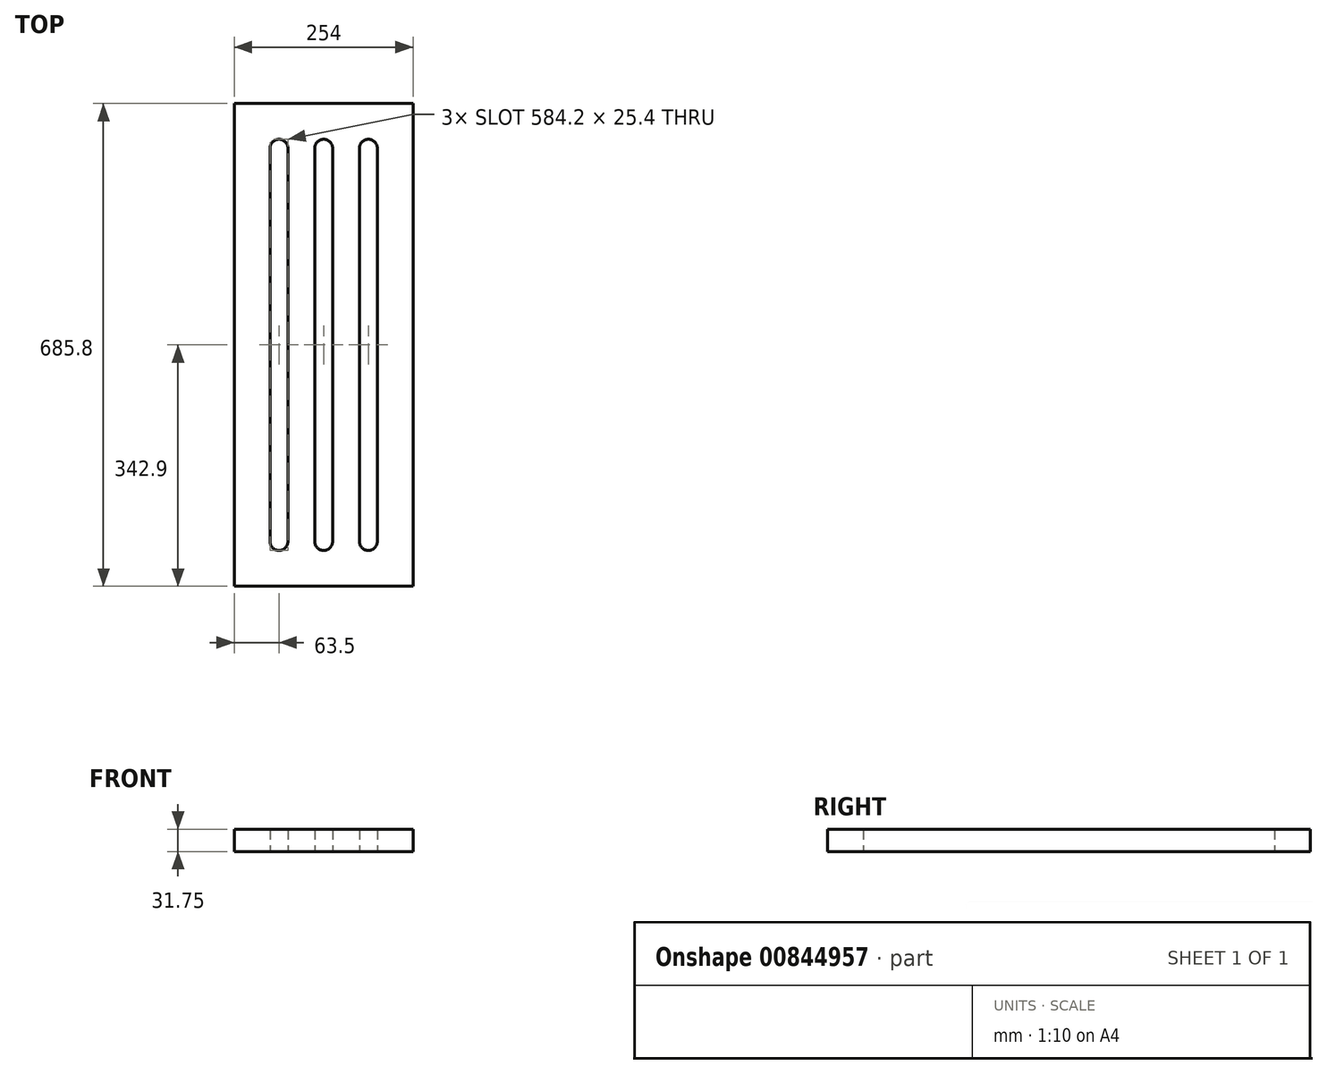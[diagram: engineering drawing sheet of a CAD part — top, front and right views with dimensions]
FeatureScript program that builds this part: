
annotation { "Feature Type Name" : "Feature", "Feature Type Description" : "" }
export const myFeature = defineFeature(function(context is Context, id is Id, definition is map)
    precondition{}
    {
        {
            var Q0;
            Q0=qCreatedBy(makeId("Top.planeOp"),FACE);
            var sketch = newSketch(context, id + "F0", { "sketchPlane" : qUnion([Q0])});
            skLineSegment(sketch, "E0.bottom", {"start": v(127, 342.9) * mm, "end": v(-127, 342.9) * mm});
            skLineSegment(sketch, "E0.top", {"start": v(127, -342.9) * mm, "end": v(-127, -342.9) * mm});
            skLineSegment(sketch, "E0.left", {"start": v(127, 342.9) * mm, "end": v(127, -342.9) * mm});
            skLineSegment(sketch, "E0.right", {"start": v(-127, 342.9) * mm, "end": v(-127, -342.9) * mm});
            skPoint(sketch, "E0.middle", {"position": v(0, 0) * mm});
            skPoint(sketch, "E1", {"position": v(-63.5, 279.4) * mm});
            skPoint(sketch, "E2", {"position": v(63.5, 279.4) * mm});
            skPoint(sketch, "E3", {"position": v(0, 279.4) * mm});
            skPoint(sketch, "E4", {"position": v(-63.5, -279.4) * mm});
            skPoint(sketch, "E5", {"position": v(0, -279.4) * mm});
            skPoint(sketch, "E6", {"position": v(63.5, -279.4) * mm});
            skCircle(sketch, "E7", {"center": v(-63.5, 279.4) * mm, "radius": 12.7 * mm});
            skCircle(sketch, "E8", {"center": v(0, 279.4) * mm, "radius": 12.7 * mm});
            skCircle(sketch, "E9", {"center": v(63.5, 279.4) * mm, "radius": 12.7 * mm});
            skCircle(sketch, "E10", {"center": v(-63.5, -279.4) * mm, "radius": 12.7 * mm});
            skCircle(sketch, "E11", {"center": v(0, -279.4) * mm, "radius": 12.7 * mm});
            skCircle(sketch, "E12", {"center": v(63.5, -279.4) * mm, "radius": 12.7 * mm});
            skLineSegment(sketch, "E13", {"start": v(-76.2, 279.4) * mm, "end": v(-76.2, -279.4) * mm});
            skLineSegment(sketch, "E14", {"start": v(-50.8, 279.4) * mm, "end": v(-50.8, -279.4) * mm});
            skLineSegment(sketch, "E15", {"start": v(-12.7, 279.4) * mm, "end": v(-12.7, -279.4) * mm});
            skLineSegment(sketch, "E16", {"start": v(12.7, 279.4) * mm, "end": v(12.7, -279.4) * mm});
            skLineSegment(sketch, "E17", {"start": v(50.8, 279.4) * mm, "end": v(50.8, -279.4) * mm});
            skLineSegment(sketch, "E18", {"start": v(76.2, 279.4) * mm, "end": v(76.2, -279.4) * mm});
            skSolve(sketch);
        }
        {
            var Q0;
            Q0 = qSketchRegion(id + "F0", true);
            extrude(context, id + "F1", {"entities" : qUnion([Q0]), "depth" : 31.75 * mm, "offsetDistance" : 25.4 * mm});
        }
    });
